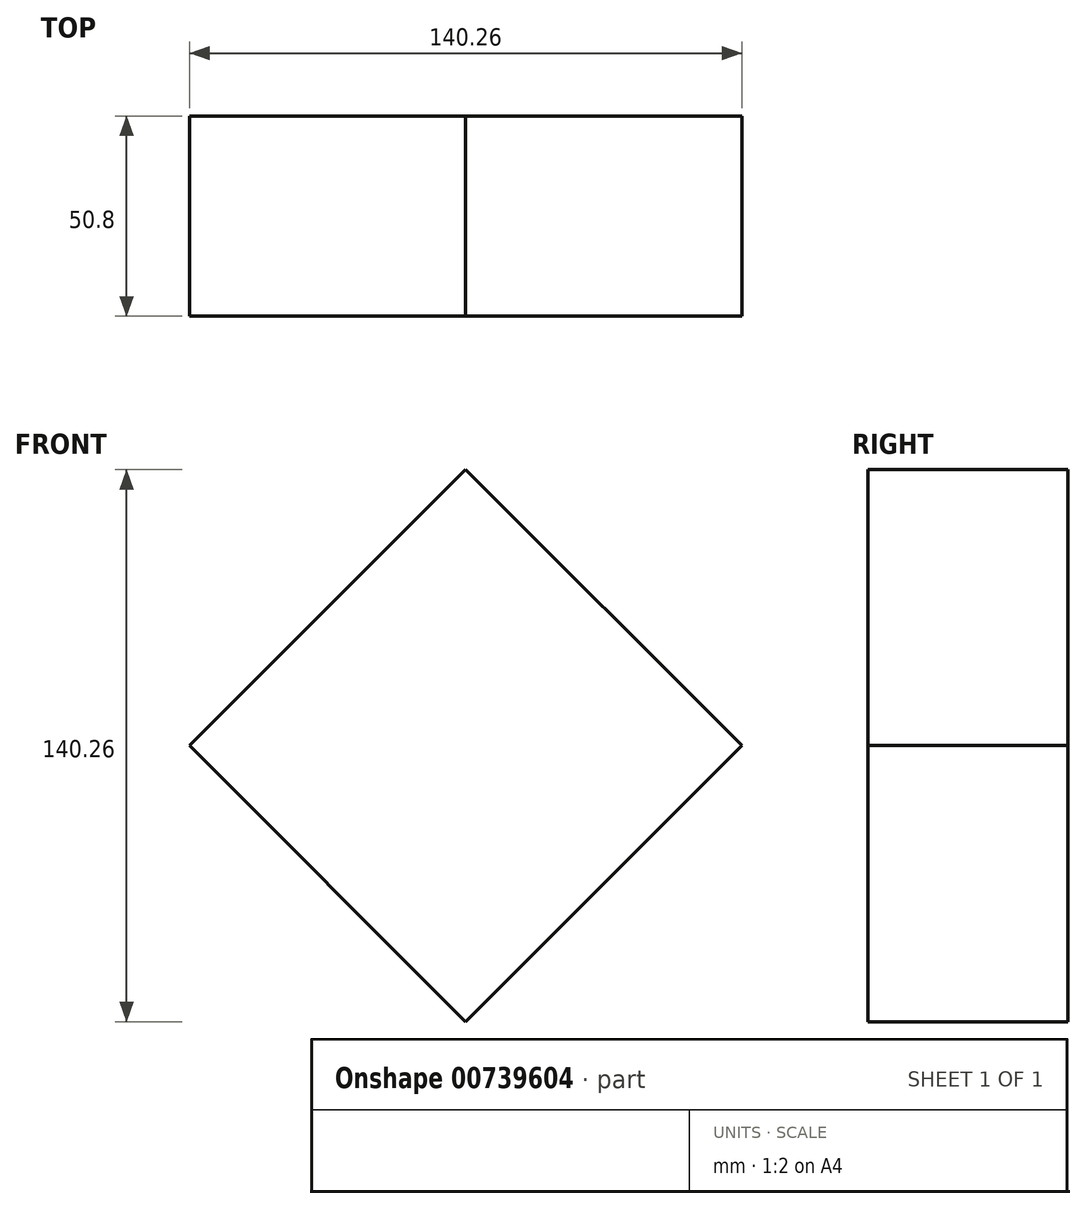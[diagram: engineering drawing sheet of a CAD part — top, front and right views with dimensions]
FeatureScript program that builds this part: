
annotation { "Feature Type Name" : "Feature", "Feature Type Description" : "" }
export const myFeature = defineFeature(function(context is Context, id is Id, definition is map)
    precondition{}
    {
        {
            var Q0;
            Q0=qCreatedBy(makeId("Front.planeOp"),FACE);
            var sketch = newSketch(context, id + "F0", { "sketchPlane" : qUnion([Q0])});
            skCircle(sketch, "E0.cCircle", {"center": v(0, 0) * mm, "radius": 70.13 * mm, "construction": true});
            skLineSegment(sketch, "E0.0", {"start": v(0, 70.13) * mm, "end": v(70.13, 0) * mm});
            skLineSegment(sketch, "E0.1", {"start": v(70.13, 0) * mm, "end": v(0, -70.13) * mm});
            skLineSegment(sketch, "E0.2", {"start": v(0, -70.13) * mm, "end": v(-70.13, 0) * mm});
            skLineSegment(sketch, "E0.3", {"start": v(-70.13, 0) * mm, "end": v(0, 70.13) * mm});
            skSolve(sketch);
        }
        {
            var Q0;
            Q0=makeQuery(id+"F0.imprint","IMPRINT",FACE,{"disambiguationData":[TD([[makeQuery(id+"F0.imprint","IMPRINT",EDGE,{"derivedFrom":sQuery(id+"F0.wireOp",EDGE,"E0.0")}),-1.0]])]});
            var sketch = newSketch(context, id + "F1", { "sketchPlane" : qUnion([Q0])});
            skSolve(sketch);
        }
        {
            var Q0;
            Q0=makeQuery(id+"F1.imprint","IMPRINT",FACE,{"disambiguationData":[TD([[makeQuery(id+"F1.imprint","IMPRINT",EDGE,{"derivedFrom":makeQuery(id+"F0.imprint","IMPRINT",EDGE,{"derivedFrom":sQuery(id+"F0.wireOp",EDGE,"E0.0")})}),-1.0]])]});
            extrude(context, id + "F2", {"entities" : qUnion([Q0]), "depth" : 25.4 * mm, "offsetDistance" : 25.4 * mm, "hasSecondDirection" : true, "secondDirectionOppositeDirection" : true, "secondDirectionDepth" : 25.4 * mm});
        }
    });
